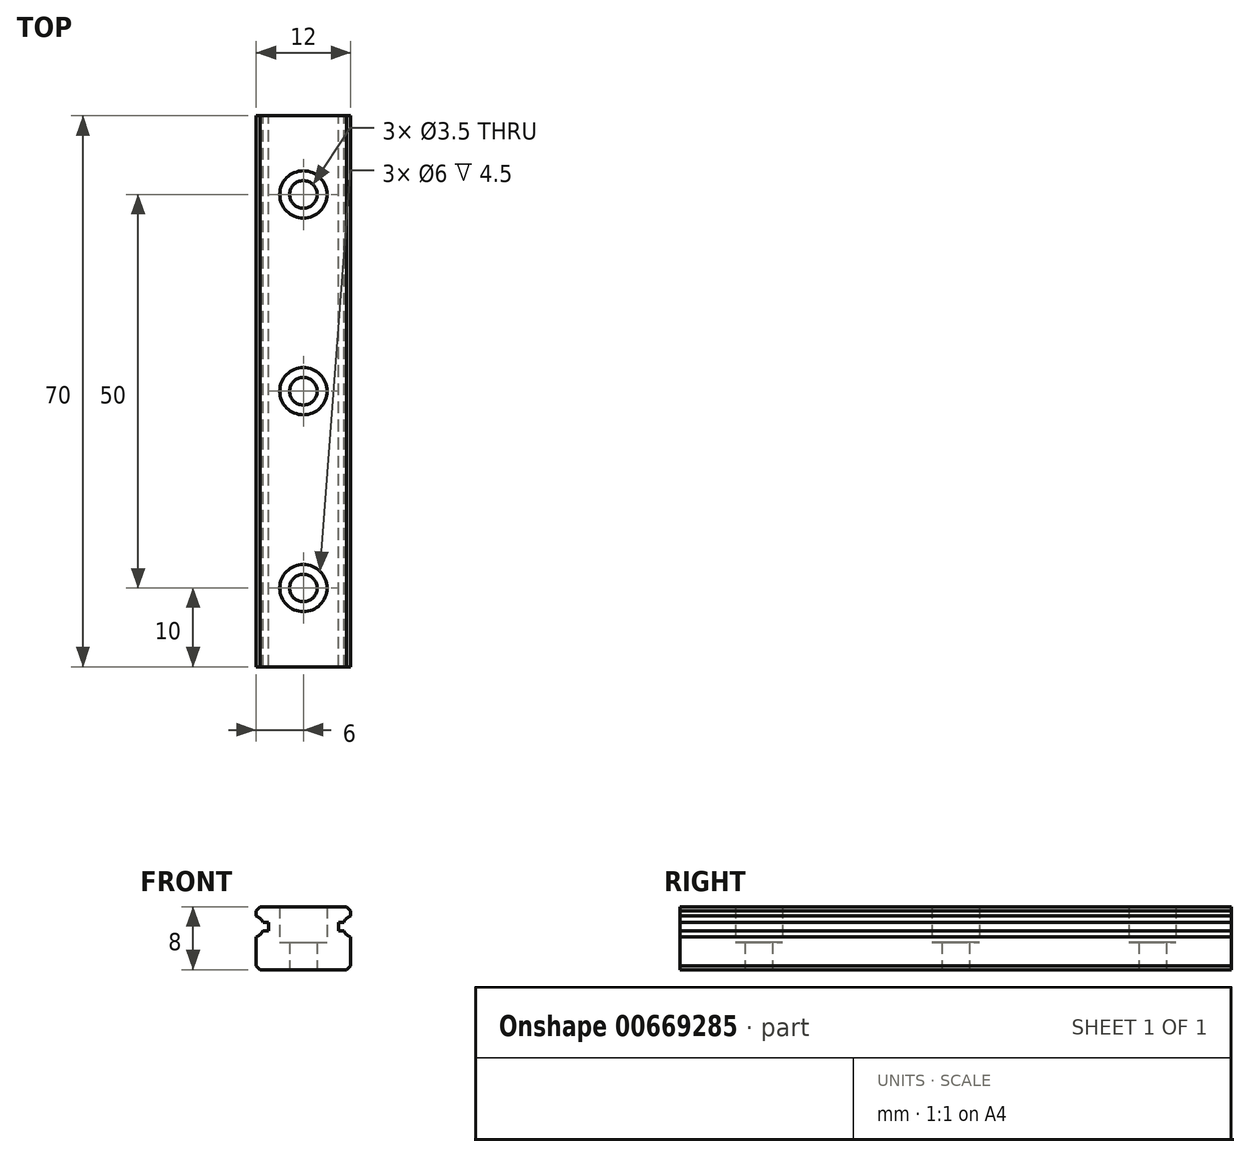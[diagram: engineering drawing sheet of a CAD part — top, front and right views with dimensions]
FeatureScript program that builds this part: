
annotation { "Feature Type Name" : "Feature", "Feature Type Description" : "" }
export const myFeature = defineFeature(function(context is Context, id is Id, definition is map)
    precondition{}
    {
        {
            var Q0;
            Q0=qCreatedBy(makeId("Front.planeOp"),FACE);
            var sketch = newSketch(context, id + "F0", { "sketchPlane" : qUnion([Q0])});
            skPoint(sketch, "E0.middle", {"position": v(0, 0) * mm});
            skLineSegment(sketch, "E1.bottom", {"start": v(5.5, -4) * mm, "end": v(-5.5, -4) * mm});
            skLineSegment(sketch, "E1.top", {"start": v(5.5, 4) * mm, "end": v(-5.5, 4) * mm});
            skLineSegment(sketch, "E1.left", {"start": v(6, -3.5) * mm, "end": v(6, 0.17) * mm});
            skLineSegment(sketch, "E1.right", {"start": v(-6, -3.5) * mm, "end": v(-6, 0.17) * mm});
            skArc(sketch, "E2", {"start": v(-6, 0.17) * mm, "mid": v(-5.5, 0.47) * mm, "end": v(-5.15, 0.95) * mm});
            skArc(sketch, "E3", {"start": v(6, 2.83) * mm, "mid": v(5.5, 2.53) * mm, "end": v(5.15, 2.05) * mm});
            skLineSegment(sketch, "E4", {"start": v(4.45, 2.05) * mm, "end": v(5.15, 2.05) * mm});
            skLineSegment(sketch, "E5", {"start": v(4.45, 0.95) * mm, "end": v(5.15, 0.95) * mm});
            skLineSegment(sketch, "E6", {"start": v(-4.45, 0.95) * mm, "end": v(-5.15, 0.95) * mm});
            skLineSegment(sketch, "E7", {"start": v(-4.45, 2.05) * mm, "end": v(-5.15, 2.05) * mm});
            skLineSegment(sketch, "E8", {"start": v(-6, 3.5) * mm, "end": v(-5.5, 4) * mm});
            skLineSegment(sketch, "E9.MirrorCS", {"start": v(6, 3.5) * mm, "end": v(5.5, 4) * mm});
            skLineSegment(sketch, "E10.MirrorCS", {"start": v(6, -3.5) * mm, "end": v(5.5, -4) * mm});
            skLineSegment(sketch, "E11.MirrorCS", {"start": v(-6, -3.5) * mm, "end": v(-5.5, -4) * mm});
            skPoint(sketch, "E12.orphan", {"position": v(-6, 4) * mm});
            skLineSegment(sketch, "E13.trimOffspring", {"start": v(-6, 2.83) * mm, "end": v(-6, 3.5) * mm});
            skArc(sketch, "E14.trimOffspring", {"start": v(-5.15, 2.05) * mm, "mid": v(-5.5, 2.53) * mm, "end": v(-6, 2.83) * mm});
            skPoint(sketch, "E15.orphan", {"position": v(6, 4) * mm});
            skLineSegment(sketch, "E16.trimOffspring", {"start": v(6, 2.83) * mm, "end": v(6, 3.5) * mm});
            skArc(sketch, "E17.trimOffspring", {"start": v(5.15, 0.95) * mm, "mid": v(5.5, 0.47) * mm, "end": v(6, 0.17) * mm});
            skPoint(sketch, "E18.orphan", {"position": v(6, -4) * mm});
            skPoint(sketch, "E19.orphan", {"position": v(-6, -4) * mm});
            skLineSegment(sketch, "E20", {"start": v(-4.45, 2.05) * mm, "end": v(-4.45, 0.95) * mm});
            skLineSegment(sketch, "E21", {"start": v(4.45, 2.05) * mm, "end": v(4.45, 0.95) * mm});
            skLineSegment(sketch, "E22", {"start": v(-6.44, 1.5) * mm, "end": v(6.44, 1.5) * mm, "construction": true});
            skSolve(sketch);
        }
        {
            var Q0;
            Q0=makeQuery(id+"F0.imprint","IMPRINT",FACE,{"disambiguationData":[TD([[makeQuery(id+"F0.imprint","IMPRINT",EDGE,{"derivedFrom":sQuery(id+"F0.wireOp",EDGE,"E1.bottom")}),-1.0]])]});
            extrude(context, id + "F1", {"entities" : qUnion([Q0]), "depth" : 70 * mm, "offsetDistance" : 25 * mm});
        }
        {
            var Q0;
            Q0=makeQuery(id+"F1.opExtrude","SWEPT_FACE",FACE,{"disambiguationData":[OSD([sQuery(id+"F0.wireOp",EDGE,"E1.top")])]});
            var sketch = newSketch(context, id + "F2", { "sketchPlane" : qUnion([Q0])});
            skPoint(sketch, "E23", {"position": v(0, -10) * mm});
            skPoint(sketch, "E24.1.0.0", {"position": v(0, -35) * mm});
            skPoint(sketch, "E24.2.0.0", {"position": v(0, -60) * mm});
            skPoint(sketch, "E24.3.0.0", {"position": v(0, -85) * mm});
            skPoint(sketch, "E24.4.0.0", {"position": v(0, -110) * mm});
            skPoint(sketch, "E24.5.0.0", {"position": v(0, -135) * mm});
            skPoint(sketch, "E24.6.0.0", {"position": v(0, -160) * mm});
            skPoint(sketch, "E24.7.0.0", {"position": v(0, -185) * mm});
            skPoint(sketch, "E24.8.0.0", {"position": v(0, -210) * mm});
            skPoint(sketch, "E24.9.0.0", {"position": v(0, -235) * mm});
            skPoint(sketch, "E24.10.0.0", {"position": v(0, -260) * mm});
            skPoint(sketch, "E24.11.0.0", {"position": v(0, -285) * mm});
            skPoint(sketch, "E24.12.0.0", {"position": v(0, -310) * mm});
            skPoint(sketch, "E24.13.0.0", {"position": v(0, -335) * mm});
            skPoint(sketch, "E24.14.0.0", {"position": v(0, -360) * mm});
            skPoint(sketch, "E24.15.0.0", {"position": v(0, -385) * mm});
            skPoint(sketch, "E24.16.0.0", {"position": v(0, -410) * mm});
            skPoint(sketch, "E24.17.0.0", {"position": v(0, -435) * mm});
            skPoint(sketch, "E24.18.0.0", {"position": v(0, -460) * mm});
            skPoint(sketch, "E24.19.0.0", {"position": v(0, -485) * mm});
            skPoint(sketch, "E24.20.0.0", {"position": v(0, -510) * mm});
            skPoint(sketch, "E24.21.0.0", {"position": v(0, -535) * mm});
            skPoint(sketch, "E24.22.0.0", {"position": v(0, -560) * mm});
            skPoint(sketch, "E24.23.0.0", {"position": v(0, -585) * mm});
            skPoint(sketch, "E24.24.0.0", {"position": v(0, -610) * mm});
            skPoint(sketch, "E24.25.0.0", {"position": v(0, -635) * mm});
            skPoint(sketch, "E24.26.0.0", {"position": v(0, -660) * mm});
            skPoint(sketch, "E24.27.0.0", {"position": v(0, -685) * mm});
            skLineSegment(sketch, "E24.direction1", {"start": v(0, -10) * mm, "end": v(0, -35) * mm, "construction": true});
            skPoint(sketch, "E25.0.28.0", {"position": v(0, -710) * mm});
            skPoint(sketch, "E25.0.29.0", {"position": v(0, -735) * mm});
            skPoint(sketch, "E25.0.30.0", {"position": v(0, -760) * mm});
            skPoint(sketch, "E25.0.31.0", {"position": v(0, -785) * mm});
            skPoint(sketch, "E25.0.32.0", {"position": v(0, -810) * mm});
            skPoint(sketch, "E25.0.33.0", {"position": v(0, -835) * mm});
            skPoint(sketch, "E25.0.34.0", {"position": v(0, -860) * mm});
            skPoint(sketch, "E25.0.35.0", {"position": v(0, -885) * mm});
            skPoint(sketch, "E25.0.36.0", {"position": v(0, -910) * mm});
            skPoint(sketch, "E25.0.37.0", {"position": v(0, -935) * mm});
            skPoint(sketch, "E25.0.38.0", {"position": v(0, -960) * mm});
            skPoint(sketch, "E25.0.39.0", {"position": v(0, -985) * mm});
            skPoint(sketch, "E25.0.40.0", {"position": v(0, -1010) * mm});
            skPoint(sketch, "E25.0.41.0", {"position": v(0, -1035) * mm});
            skPoint(sketch, "E25.0.42.0", {"position": v(0, -1060) * mm});
            skPoint(sketch, "E25.0.43.0", {"position": v(0, -1085) * mm});
            skPoint(sketch, "E25.0.44.0", {"position": v(0, -1110) * mm});
            skPoint(sketch, "E25.0.45.0", {"position": v(0, -1135) * mm});
            skPoint(sketch, "E25.0.46.0", {"position": v(0, -1160) * mm});
            skPoint(sketch, "E25.0.47.0", {"position": v(0, -1185) * mm});
            skPoint(sketch, "E25.0.48.0", {"position": v(0, -1210) * mm});
            skPoint(sketch, "E25.0.49.0", {"position": v(0, -1235) * mm});
            skPoint(sketch, "E25.0.50.0", {"position": v(0, -1260) * mm});
            skPoint(sketch, "E25.0.51.0", {"position": v(0, -1285) * mm});
            skPoint(sketch, "E25.0.52.0", {"position": v(0, -1310) * mm});
            skPoint(sketch, "E25.0.53.0", {"position": v(0, -1335) * mm});
            skPoint(sketch, "E25.0.54.0", {"position": v(0, -1360) * mm});
            skPoint(sketch, "E25.0.55.0", {"position": v(0, -1385) * mm});
            skPoint(sketch, "E25.0.56.0", {"position": v(0, -1410) * mm});
            skPoint(sketch, "E25.0.57.0", {"position": v(0, -1435) * mm});
            skPoint(sketch, "E25.0.58.0", {"position": v(0, -1460) * mm});
            skPoint(sketch, "E25.0.59.0", {"position": v(0, -1485) * mm});
            skPoint(sketch, "E25.0.60.0", {"position": v(0, -1510) * mm});
            skPoint(sketch, "E25.0.61.0", {"position": v(0, -1535) * mm});
            skPoint(sketch, "E25.0.62.0", {"position": v(0, -1560) * mm});
            skPoint(sketch, "E25.0.63.0", {"position": v(0, -1585) * mm});
            skPoint(sketch, "E25.0.64.0", {"position": v(0, -1610) * mm});
            skPoint(sketch, "E25.0.65.0", {"position": v(0, -1635) * mm});
            skPoint(sketch, "E25.0.66.0", {"position": v(0, -1660) * mm});
            skPoint(sketch, "E25.0.67.0", {"position": v(0, -1685) * mm});
            skPoint(sketch, "E25.0.68.0", {"position": v(0, -1710) * mm});
            skPoint(sketch, "E25.0.69.0", {"position": v(0, -1735) * mm});
            skPoint(sketch, "E25.0.70.0", {"position": v(0, -1760) * mm});
            skPoint(sketch, "E25.0.71.0", {"position": v(0, -1785) * mm});
            skPoint(sketch, "E25.0.72.0", {"position": v(0, -1810) * mm});
            skPoint(sketch, "E25.0.73.0", {"position": v(0, -1835) * mm});
            skPoint(sketch, "E25.0.74.0", {"position": v(0, -1860) * mm});
            skPoint(sketch, "E25.0.75.0", {"position": v(0, -1885) * mm});
            skPoint(sketch, "E25.0.76.0", {"position": v(0, -1910) * mm});
            skPoint(sketch, "E25.0.77.0", {"position": v(0, -1935) * mm});
            skPoint(sketch, "E25.0.78.0", {"position": v(0, -1960) * mm});
            skPoint(sketch, "E25.0.79.0", {"position": v(0, -1985) * mm});
            skSolve(sketch);
        }
        {
            var Q0;
            Q0=sQuery(id+"F2.wireOp",VERTEX,"E25.0.51.0");
            var Q1;
            Q1=sQuery(id+"F2.wireOp",VERTEX,"E25.0.44.0");
            var Q2;
            Q2=sQuery(id+"F2.wireOp",VERTEX,"E25.0.60.0");
            var Q3;
            Q3=sQuery(id+"F2.wireOp",VERTEX,"E25.0.67.0");
            var Q4;
            Q4=sQuery(id+"F2.wireOp",VERTEX,"E25.0.76.0");
            var Q5;
            Q5=sQuery(id+"F2.wireOp",VERTEX,"E24.18.0.0");
            var Q6;
            Q6=sQuery(id+"F2.wireOp",VERTEX,"E25.0.30.0");
            var Q7;
            Q7=sQuery(id+"F2.wireOp",VERTEX,"E25.0.34.0");
            var Q8;
            Q8=sQuery(id+"F2.wireOp",VERTEX,"E25.0.52.0");
            var Q9;
            Q9=sQuery(id+"F2.wireOp",VERTEX,"E25.0.45.0");
            var Q10;
            Q10=sQuery(id+"F2.wireOp",VERTEX,"E25.0.61.0");
            var Q11;
            Q11=sQuery(id+"F2.wireOp",VERTEX,"E25.0.68.0");
            var Q12;
            Q12=sQuery(id+"F2.wireOp",VERTEX,"E24.19.0.0");
            var Q13;
            Q13=sQuery(id+"F2.wireOp",VERTEX,"E25.0.77.0");
            var Q14;
            Q14=sQuery(id+"F2.wireOp",VERTEX,"E25.0.35.0");
            var Q15;
            Q15=sQuery(id+"F2.wireOp",VERTEX,"E25.0.28.0");
            var Q16;
            Q16=sQuery(id+"F2.wireOp",VERTEX,"E24.20.0.0");
            var Q17;
            Q17=sQuery(id+"F2.wireOp",VERTEX,"E25.0.36.0");
            var Q18;
            Q18=sQuery(id+"F2.wireOp",VERTEX,"E24.25.0.0");
            var Q19;
            Q19=sQuery(id+"F2.wireOp",VERTEX,"E25.0.41.0");
            var Q20;
            Q20=sQuery(id+"F2.wireOp",VERTEX,"E25.0.57.0");
            var Q21;
            Q21=sQuery(id+"F2.wireOp",VERTEX,"E25.0.73.0");
            var Q22;
            Q22=sQuery(id+"F2.wireOp",VERTEX,"E25.0.47.0");
            var Q23;
            Q23=sQuery(id+"F2.wireOp",VERTEX,"E25.0.63.0");
            var Q24;
            Q24=sQuery(id+"F2.wireOp",VERTEX,"E25.0.79.0");
            var Q25;
            Q25=sQuery(id+"F2.wireOp",VERTEX,"E24.11.0.0");
            var Q26;
            Q26=sQuery(id+"F2.wireOp",VERTEX,"E24.15.0.0");
            var Q27;
            Q27=sQuery(id+"F2.wireOp",VERTEX,"E24.10.0.0");
            var Q28;
            Q28=sQuery(id+"F2.wireOp",VERTEX,"E24.9.0.0");
            var Q29;
            Q29=sQuery(id+"F2.wireOp",VERTEX,"E24.8.0.0");
            var Q30;
            Q30=sQuery(id+"F2.wireOp",VERTEX,"E24.2.0.0");
            var Q31;
            Q31=sQuery(id+"F2.wireOp",VERTEX,"E24.1.0.0");
            var Q32;
            Q32=sQuery(id+"F2.wireOp",VERTEX,"E25.0.37.0");
            var Q33;
            Q33=sQuery(id+"F2.wireOp",VERTEX,"E24.7.0.0");
            var Q34;
            Q34=sQuery(id+"F2.wireOp",VERTEX,"E25.0.69.0");
            var Q35;
            Q35=sQuery(id+"F2.wireOp",VERTEX,"E25.0.53.0");
            var Q36;
            Q36=sQuery(id+"F2.wireOp",VERTEX,"E23");
            var Q37;
            Q37=sQuery(id+"F2.wireOp",VERTEX,"E24.3.0.0");
            var Q38;
            Q38=sQuery(id+"F2.wireOp",VERTEX,"E24.4.0.0");
            var Q39;
            Q39=sQuery(id+"F2.wireOp",VERTEX,"E24.6.0.0");
            var Q40;
            Q40=sQuery(id+"F2.wireOp",VERTEX,"E24.5.0.0");
            var Q41;
            Q41=sQuery(id+"F2.wireOp",VERTEX,"E24.21.0.0");
            var Q42;
            Q42=sQuery(id+"F2.wireOp",VERTEX,"E25.0.29.0");
            var Q43;
            Q43=sQuery(id+"F2.wireOp",VERTEX,"E24.26.0.0");
            var Q44;
            Q44=sQuery(id+"F2.wireOp",VERTEX,"E25.0.42.0");
            var Q45;
            Q45=sQuery(id+"F2.wireOp",VERTEX,"E25.0.58.0");
            var Q46;
            Q46=sQuery(id+"F2.wireOp",VERTEX,"E25.0.74.0");
            var Q47;
            Q47=sQuery(id+"F2.wireOp",VERTEX,"E25.0.43.0");
            var Q48;
            Q48=sQuery(id+"F2.wireOp",VERTEX,"E25.0.59.0");
            var Q49;
            Q49=sQuery(id+"F2.wireOp",VERTEX,"E25.0.75.0");
            var Q50;
            Q50=sQuery(id+"F2.wireOp",VERTEX,"E25.0.48.0");
            var Q51;
            Q51=sQuery(id+"F2.wireOp",VERTEX,"E25.0.64.0");
            var Q52;
            Q52=sQuery(id+"F2.wireOp",VERTEX,"E25.0.31.0");
            var Q53;
            Q53=sQuery(id+"F2.wireOp",VERTEX,"E25.0.49.0");
            var Q54;
            Q54=sQuery(id+"F2.wireOp",VERTEX,"E25.0.65.0");
            var Q55;
            Q55=sQuery(id+"F2.wireOp",VERTEX,"E24.16.0.0");
            var Q56;
            Q56=sQuery(id+"F2.wireOp",VERTEX,"E25.0.32.0");
            var Q57;
            Q57=sQuery(id+"F2.wireOp",VERTEX,"E25.0.50.0");
            var Q58;
            Q58=sQuery(id+"F2.wireOp",VERTEX,"E25.0.46.0");
            var Q59;
            Q59=sQuery(id+"F2.wireOp",VERTEX,"E25.0.66.0");
            var Q60;
            Q60=sQuery(id+"F2.wireOp",VERTEX,"E25.0.62.0");
            var Q61;
            Q61=sQuery(id+"F2.wireOp",VERTEX,"E24.17.0.0");
            var Q62;
            Q62=sQuery(id+"F2.wireOp",VERTEX,"E25.0.78.0");
            var Q63;
            Q63=sQuery(id+"F2.wireOp",VERTEX,"E24.22.0.0");
            var Q64;
            Q64=sQuery(id+"F2.wireOp",VERTEX,"E25.0.33.0");
            var Q65;
            Q65=sQuery(id+"F2.wireOp",VERTEX,"E24.13.0.0");
            var Q66;
            Q66=sQuery(id+"F2.wireOp",VERTEX,"E25.0.70.0");
            var Q67;
            Q67=sQuery(id+"F2.wireOp",VERTEX,"E25.0.54.0");
            var Q68;
            Q68=sQuery(id+"F2.wireOp",VERTEX,"E24.12.0.0");
            var Q69;
            Q69=sQuery(id+"F2.wireOp",VERTEX,"E25.0.38.0");
            var Q70;
            Q70=sQuery(id+"F2.wireOp",VERTEX,"E24.27.0.0");
            var Q71;
            Q71=sQuery(id+"F2.wireOp",VERTEX,"E25.0.39.0");
            var Q72;
            Q72=sQuery(id+"F2.wireOp",VERTEX,"E25.0.56.0");
            var Q73;
            Q73=sQuery(id+"F2.wireOp",VERTEX,"E25.0.40.0");
            var Q74;
            Q74=sQuery(id+"F2.wireOp",VERTEX,"E25.0.72.0");
            var Q75;
            Q75=sQuery(id+"F2.wireOp",VERTEX,"E24.23.0.0");
            var Q76;
            Q76=sQuery(id+"F2.wireOp",VERTEX,"E25.0.55.0");
            var Q77;
            Q77=sQuery(id+"F2.wireOp",VERTEX,"E24.14.0.0");
            var Q78;
            Q78=sQuery(id+"F2.wireOp",VERTEX,"E25.0.71.0");
            var Q79;
            Q79=sQuery(id+"F2.wireOp",VERTEX,"E24.24.0.0");
            var Q80;
            Q80=makeQuery(id+"F1.opExtrude","SWEPT_BODY",BODY,{"disambiguationData":[OSD([sQuery(id+"F0.wireOp",EDGE,"E1.bottom"),sQuery(id+"F0.wireOp",EDGE,"E1.top"),sQuery(id+"F0.wireOp",EDGE,"E1.left"),sQuery(id+"F0.wireOp",EDGE,"E1.right"),sQuery(id+"F0.wireOp",EDGE,"E2"),sQuery(id+"F0.wireOp",EDGE,"E3"),sQuery(id+"F0.wireOp",EDGE,"E4"),sQuery(id+"F0.wireOp",EDGE,"E5"),sQuery(id+"F0.wireOp",EDGE,"E6"),sQuery(id+"F0.wireOp",EDGE,"E7"),sQuery(id+"F0.wireOp",EDGE,"E8"),sQuery(id+"F0.wireOp",EDGE,"E9.MirrorCS"),sQuery(id+"F0.wireOp",EDGE,"E10.MirrorCS"),sQuery(id+"F0.wireOp",EDGE,"E11.MirrorCS"),sQuery(id+"F0.wireOp",EDGE,"E13.trimOffspring"),sQuery(id+"F0.wireOp",EDGE,"E14.trimOffspring"),sQuery(id+"F0.wireOp",EDGE,"E16.trimOffspring"),sQuery(id+"F0.wireOp",EDGE,"E17.trimOffspring"),sQuery(id+"F0.wireOp",EDGE,"E20"),sQuery(id+"F0.wireOp",EDGE,"E21")])]});
            hole(context, id + "F3", {"style" : HoleStyle.C_BORE, "endStyle" : HoleEndStyle.THROUGH, "holeDiameter" : 3.5 * mm, "cBoreDiameter" : 6 * mm, "cBoreDepth" : 4.5 * mm, "majorDiameter" : 5 * mm, "isTappedThrough" : true, "tappedDepth" : 12 * mm, "tapClearance" : 3, "locations" : qUnion([Q0, Q1, Q2, Q3, Q4, Q5, Q6, Q7, Q8, Q9, Q10, Q11, Q12, Q13, Q14, Q15, Q16, Q17, Q18, Q19, Q20, Q21, Q22, Q23, Q24, Q25, Q26, Q27, Q28, Q29, Q30, Q31, Q32, Q33, Q34, Q35, Q36, Q37, Q38, Q39, Q40, Q41, Q42, Q43, Q44, Q45, Q46, Q47, Q48, Q49, Q50, Q51, Q52, Q53, Q54, Q55, Q56, Q57, Q58, Q59, Q60, Q61, Q62, Q63, Q64, Q65, Q66, Q67, Q68, Q69, Q70, Q71, Q72, Q73, Q74, Q75, Q76, Q77, Q78, Q79]), "scope" : qUnion([Q80]), "startStyle" : HoleStartStyle.PART});
        }
    });
